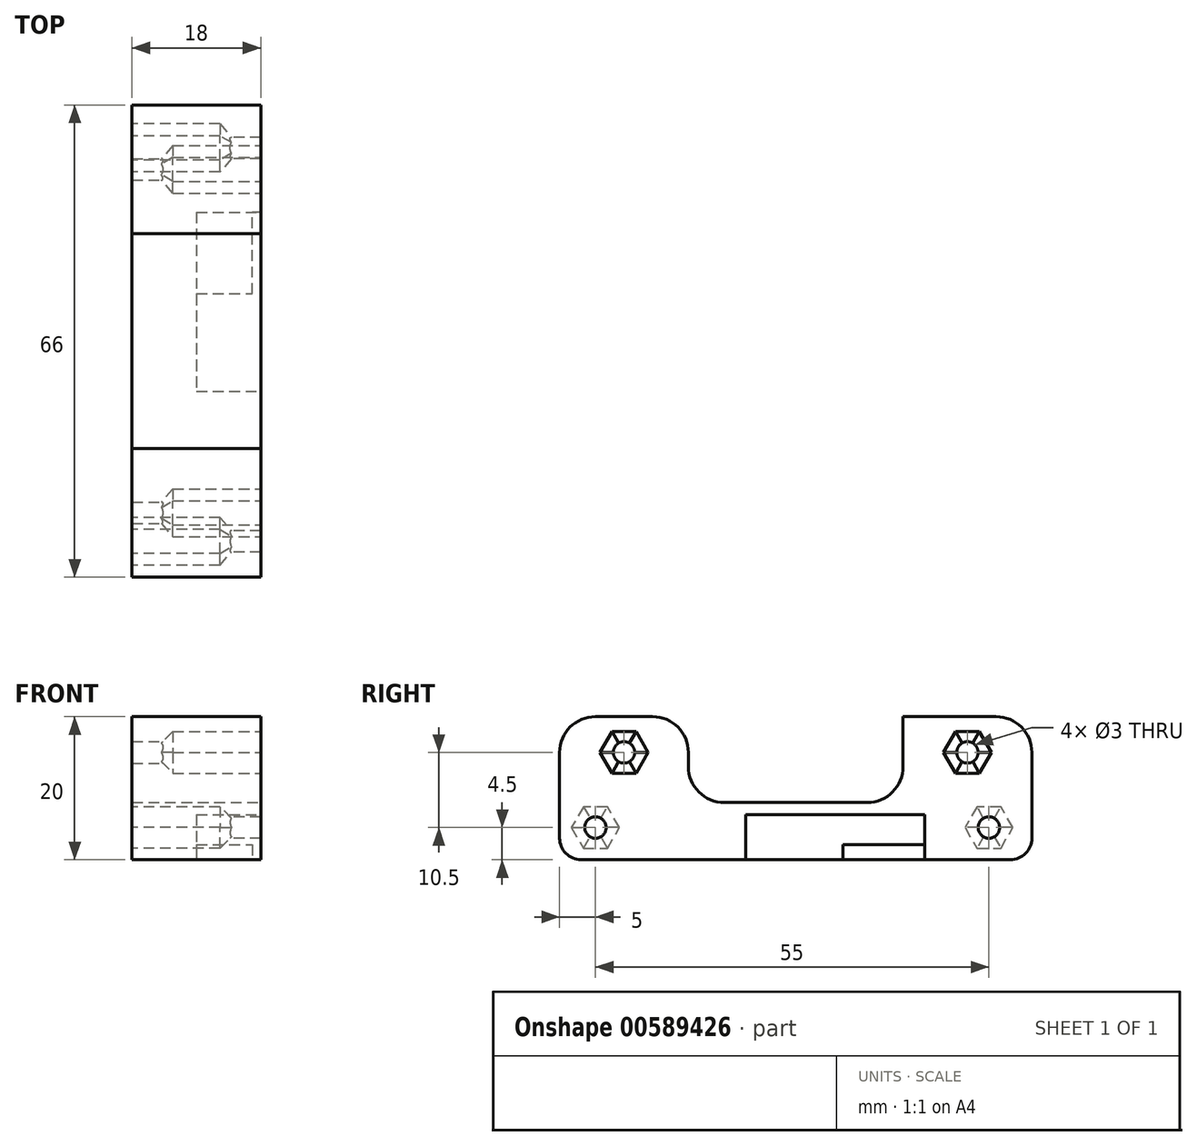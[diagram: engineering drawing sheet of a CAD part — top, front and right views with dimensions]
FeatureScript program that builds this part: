
annotation { "Feature Type Name" : "Feature", "Feature Type Description" : "" }
export const myFeature = defineFeature(function(context is Context, id is Id, definition is map)
    precondition{}
    {
        {
            var Q0;
            Q0=qCreatedBy(makeId("Right.planeOp"),FACE);
            var sketch = newSketch(context, id + "F0", { "sketchPlane" : qUnion([Q0])});
            skLineSegment(sketch, "E0", {"start": v(0, 0) * mm, "end": v(0, 20) * mm});
            skLineSegment(sketch, "E1", {"start": v(0, 20) * mm, "end": v(10, 20) * mm});
            skLineSegment(sketch, "E2", {"start": v(10, 20) * mm, "end": v(10, 18) * mm});
            skLineSegment(sketch, "E3", {"start": v(10, 18) * mm, "end": v(5, 18) * mm});
            skLineSegment(sketch, "E4", {"start": v(5, 18) * mm, "end": v(5, 9) * mm});
            skLineSegment(sketch, "E5", {"start": v(5, 9) * mm, "end": v(66, 9) * mm});
            skLineSegment(sketch, "E6", {"start": v(66, 9) * mm, "end": v(66, 0) * mm});
            skLineSegment(sketch, "E7", {"start": v(66, 0) * mm, "end": v(0, 0) * mm});
            skLineSegment(sketch, "E8", {"start": v(66, 9) * mm, "end": v(66, 20) * mm});
            skLineSegment(sketch, "E9", {"start": v(66, 20) * mm, "end": v(10, 20) * mm});
            skSolve(sketch);
        }
        {
            var Q0;
            Q0=makeQuery(id+"F0.imprint","IMPRINT",FACE,{"disambiguationData":[TD([[makeQuery(id+"F0.imprint","IMPRINT",EDGE,{"derivedFrom":sQuery(id+"F0.wireOp",EDGE,"E0")}),-1.0]])]});
            var Q1;
            Q1=makeQuery(id+"F0.imprint","IMPRINT",FACE,{"disambiguationData":[TD([[makeQuery(id+"F0.imprint","IMPRINT",EDGE,{"derivedFrom":sQuery(id+"F0.wireOp",EDGE,"E2")}),1.0]])]});
            extrude(context, id + "F1", {"entities" : qUnion([Q0, Q1]), "oppositeDirection" : true, "depth" : 16 * mm, "offsetDistance" : 25 * mm});
        }
        {
            var Q0;
            Q0=makeQuery(id+"F1.opExtrude","CAP_FACE",FACE,{"disambiguationData":[OSD([sQuery(id+"F0.wireOp",EDGE,"E0"),sQuery(id+"F0.wireOp",EDGE,"E1"),sQuery(id+"F0.wireOp",EDGE,"E6"),sQuery(id+"F0.wireOp",EDGE,"E7"),sQuery(id+"F0.wireOp",EDGE,"E8"),sQuery(id+"F0.wireOp",EDGE,"E9")])],"isStart":true});
            var sketch = newSketch(context, id + "F2", { "sketchPlane" : qUnion([Q0])});
            skLineSegment(sketch, "E10", {"start": v(51, 6.3) * mm, "end": v(51, 2.1) * mm});
            skLineSegment(sketch, "E11", {"start": v(51, 2.1) * mm, "end": v(39.6, 2.1) * mm});
            skLineSegment(sketch, "E12", {"start": v(39.6, 2.1) * mm, "end": v(39.6, 0) * mm});
            skLineSegment(sketch, "E13", {"start": v(51, 6.3) * mm, "end": v(26, 6.3) * mm});
            skLineSegment(sketch, "E14", {"start": v(26, 6.3) * mm, "end": v(26, 0) * mm});
            skLineSegment(sketch, "E15.0", {"start": v(66, 0) * mm, "end": v(0, 0) * mm});
            skSolve(sketch);
        }
        {
            var Q0;
            Q0=makeQuery(id+"F2.imprint","IMPRINT",FACE,{"disambiguationData":[TD([[makeQuery(id+"F2.imprint","IMPRINT",EDGE,{"derivedFrom":sQuery(id+"F2.wireOp",EDGE,"E10")}),-1.0]])]});
            extrude(context, id + "F3", {"entities" : qUnion([Q0]), "operationType" : NewBodyOperationType.REMOVE, "oppositeDirection" : true, "depth" : 9 * mm, "offsetDistance" : 25 * mm});
        }
        {
            var Q0;
            Q0=makeQuery(id+"F1.opExtrude","SWEPT_FACE",FACE,{"disambiguationData":[OSD([sQuery(id+"F0.wireOp",EDGE,"E7")])]});
            var sketch = newSketch(context, id + "F4", { "sketchPlane" : qUnion([Q0])});
            skLineSegment(sketch, "E16.0", {"start": v(0, -66) * mm, "end": v(0, -39.6) * mm});
            skLineSegment(sketch, "E17.bottom", {"start": v(0, -39.6) * mm, "end": v(-1.2, -39.6) * mm});
            skLineSegment(sketch, "E17.top", {"start": v(0, -51) * mm, "end": v(-1.2, -51) * mm});
            skLineSegment(sketch, "E17.left", {"start": v(0, -39.6) * mm, "end": v(0, -51) * mm});
            skLineSegment(sketch, "E17.right", {"start": v(-1.2, -39.6) * mm, "end": v(-1.2, -51) * mm});
            skPoint(sketch, "E18.0", {"position": v(0, -51) * mm});
            skSolve(sketch);
        }
        {
            var Q0;
            Q0=makeQuery(id+"F4.imprint","IMPRINT",FACE,{"disambiguationData":[TD([[makeQuery(id+"F4.imprint","IMPRINT",EDGE,{"derivedFrom":sQuery(id+"F4.wireOp",EDGE,"E17.bottom")}),-1.0]])]});
            extrude(context, id + "F5", {"entities" : qUnion([Q0]), "operationType" : NewBodyOperationType.REMOVE, "endBound" : BoundingType.UP_TO_NEXT, "oppositeDirection" : true, "depth" : 25 * mm, "offsetDistance" : 25 * mm});
        }
        {
            var Q0;
            Q0=makeQuery(id+"F1.opExtrude","CAP_FACE",FACE,{"disambiguationData":[OSD([sQuery(id+"F0.wireOp",EDGE,"E0"),sQuery(id+"F0.wireOp",EDGE,"E1"),sQuery(id+"F0.wireOp",EDGE,"E2"),sQuery(id+"F0.wireOp",EDGE,"E3"),sQuery(id+"F0.wireOp",EDGE,"E4"),sQuery(id+"F0.wireOp",EDGE,"E5"),sQuery(id+"F0.wireOp",EDGE,"E6"),sQuery(id+"F0.wireOp",EDGE,"E7")])],"isStart":false});
            var sketch = newSketch(context, id + "F6", { "sketchPlane" : qUnion([Q0])});
            skLineSegment(sketch, "E19.0", {"start": v(-66, 0) * mm, "end": v(0, 0) * mm});
            skLineSegment(sketch, "E20.0", {"start": v(0, 0) * mm, "end": v(0, 20) * mm});
            skLineSegment(sketch, "E21", {"start": v(-66, 0) * mm, "end": v(-66, 20) * mm});
            skLineSegment(sketch, "E22", {"start": v(-66, 20) * mm, "end": v(0, 20) * mm});
            skSolve(sketch);
        }
        {
            var Q0;
            {var subQ2=sQuery(id+"F6.wireOp",EDGE,"E19.0");Q0=makeQuery(id+"F6.imprint","IMPRINT",FACE,{"disambiguationData":[TD([[makeQuery(id+"F6.imprint","IMPRINT",EDGE,{"derivedFrom":subQ2}),1.0]])]});}
            var Q1;
            {var subQ0=makeQuery(id+"F1.opExtrude","CAP_EDGE",EDGE,{"disambiguationData":[OSD([sQuery(id+"F0.wireOp",EDGE,"E2")])],"isStart":false});Q1=makeQuery(id+"F6.imprint","IMPRINT",FACE,{"disambiguationData":[TD([[makeQuery(id+"F6.imprint","IMPRINT",EDGE,{"derivedFrom":subQ0}),-1.0]])]});}
            extrude(context, id + "F7", {"entities" : qUnion([Q0, Q1]), "operationType" : NewBodyOperationType.ADD, "depth" : 2 * mm, "offsetDistance" : 25 * mm});
        }
        {
            var Q0;
            Q0=makeQuery(id+"F7.boolean.opBoolean","MERGE",EDGE,{"derivedFrom":[makeQuery(id+"F1.opExtrude","SWEPT_EDGE",EDGE,{"disambiguationData":[OSD([sQuery(id+"F0.wireOp",EDGE,"E6"),sQuery(id+"F0.wireOp",EDGE,"E7")])]}),makeQuery(id+"F7.opExtrude","SWEPT_EDGE",EDGE,{"disambiguationData":[OSD([sQuery(id+"F6.wireOp",EDGE,"E19.0"),sQuery(id+"F6.wireOp",EDGE,"E21")])]})]});
            var Q1;
            Q1=makeQuery(id+"Faa1i12ZNwMVlYs_1.boolean.opBoolean","COPY",EDGE,{"derivedFrom":makeQuery(id+"Faa1i12ZNwMVlYs_1.opExtrude","SWEPT_EDGE",EDGE,{"disambiguationData":[OSD([sQuery(id+"FbflpkZ62X0eoyx_1.wireOp",EDGE,"95200aa5-3b6f-4f71-a4fa-d7a12fe171fd.0"),sQuery(id+"FbflpkZ62X0eoyx_1.wireOp",EDGE,"u4Z3bOsj-DbHr-OVNa-PfcN-1bMwixkQpOJ3")])]})});
            var Q2;
            Q2=makeQuery(id+"F7.boolean.opBoolean","MERGE",EDGE,{"derivedFrom":[makeQuery(id+"F1.opExtrude","SWEPT_EDGE",EDGE,{"disambiguationData":[OSD([sQuery(id+"F0.wireOp",EDGE,"E0"),sQuery(id+"F0.wireOp",EDGE,"E7")])]}),makeQuery(id+"F7.opExtrude","SWEPT_EDGE",EDGE,{"disambiguationData":[OSD([sQuery(id+"F6.wireOp",EDGE,"E19.0"),sQuery(id+"F6.wireOp",EDGE,"E20.0")])]})]});
            fillet(context, id + "F8", {"entities" : qUnion([Q0, Q1, Q2]), "radius" : 3 * mm, "tangentPropagation" : true, "allowEdgeOverflow" : false});
        }
        {
            var Q0;
            Q0=makeQuery(id+"F7.opExtrude","CAP_FACE",FACE,{"disambiguationData":[OSD([sQuery(id+"F6.wireOp",EDGE,"E19.0"),sQuery(id+"F6.wireOp",EDGE,"E20.0"),sQuery(id+"F6.wireOp",EDGE,"E21"),sQuery(id+"F6.wireOp",EDGE,"E22")])],"isStart":false});
            var sketch = newSketch(context, id + "F9", { "sketchPlane" : qUnion([Q0])});
            skCircle(sketch, "E23.cCircle", {"center": v(-60, 4.5) * mm, "radius": 2.9 * mm, "construction": true});
            skLineSegment(sketch, "E23.0", {"start": v(-63.35, 4.5) * mm, "end": v(-61.67, 7.4) * mm});
            skLineSegment(sketch, "E23.1", {"start": v(-61.67, 7.4) * mm, "end": v(-58.33, 7.4) * mm});
            skLineSegment(sketch, "E23.2", {"start": v(-58.33, 7.4) * mm, "end": v(-56.65, 4.5) * mm});
            skLineSegment(sketch, "E23.3", {"start": v(-56.65, 4.5) * mm, "end": v(-58.33, 1.6) * mm});
            skLineSegment(sketch, "E23.4", {"start": v(-58.33, 1.6) * mm, "end": v(-61.67, 1.6) * mm});
            skLineSegment(sketch, "E23.5", {"start": v(-61.67, 1.6) * mm, "end": v(-63.35, 4.5) * mm});
            skPoint(sketch, "E23.0.midPoint", {"position": v(-62.51, 5.95) * mm});
            skLineSegment(sketch, "E24.1.0.0", {"start": v(-6.67, 1.6) * mm, "end": v(-8.35, 4.5) * mm});
            skPoint(sketch, "E24.1.0.1", {"position": v(-7.51, 5.95) * mm});
            skCircle(sketch, "E24.1.0.2", {"center": v(-5, 4.5) * mm, "radius": 2.9 * mm, "construction": true});
            skLineSegment(sketch, "E24.1.0.3", {"start": v(-8.35, 4.5) * mm, "end": v(-6.67, 7.4) * mm});
            skLineSegment(sketch, "E24.1.0.4", {"start": v(-6.67, 7.4) * mm, "end": v(-3.33, 7.4) * mm});
            skLineSegment(sketch, "E24.1.0.5", {"start": v(-3.33, 7.4) * mm, "end": v(-1.65, 4.5) * mm});
            skLineSegment(sketch, "E24.1.0.6", {"start": v(-1.65, 4.5) * mm, "end": v(-3.33, 1.6) * mm});
            skLineSegment(sketch, "E24.1.0.7", {"start": v(-3.33, 1.6) * mm, "end": v(-6.67, 1.6) * mm});
            skLineSegment(sketch, "E24.2.0.0", {"start": v(48.33, 1.6) * mm, "end": v(46.65, 4.5) * mm});
            skPoint(sketch, "E24.2.0.1", {"position": v(47.49, 5.95) * mm});
            skCircle(sketch, "E24.2.0.2", {"center": v(50, 4.5) * mm, "radius": 2.9 * mm, "construction": true});
            skLineSegment(sketch, "E24.2.0.3", {"start": v(46.65, 4.5) * mm, "end": v(48.33, 7.4) * mm});
            skLineSegment(sketch, "E24.2.0.4", {"start": v(48.33, 7.4) * mm, "end": v(51.67, 7.4) * mm});
            skLineSegment(sketch, "E24.2.0.5", {"start": v(51.67, 7.4) * mm, "end": v(53.35, 4.5) * mm});
            skLineSegment(sketch, "E24.2.0.6", {"start": v(53.35, 4.5) * mm, "end": v(51.67, 1.6) * mm});
            skLineSegment(sketch, "E24.2.0.7", {"start": v(51.67, 1.6) * mm, "end": v(48.33, 1.6) * mm});
            skLineSegment(sketch, "E24.direction1", {"start": v(-61.67, 1.6) * mm, "end": v(-6.67, 1.6) * mm, "construction": true});
            skSolve(sketch);
        }
        {
            var Q0;
            Q0=makeQuery(id+"F9.imprint","IMPRINT",FACE,{"disambiguationData":[TD([[makeQuery(id+"F9.imprint","IMPRINT",EDGE,{"derivedFrom":sQuery(id+"F9.wireOp",EDGE,"E23.0")}),-1.0]])]});
            var Q1;
            Q1=makeQuery(id+"F9.imprint","IMPRINT",FACE,{"disambiguationData":[TD([[makeQuery(id+"F9.imprint","IMPRINT",EDGE,{"derivedFrom":sQuery(id+"F9.wireOp",EDGE,"E24.1.0.0")}),-1.0]])]});
            extrude(context, id + "F10", {"entities" : qUnion([Q0, Q1]), "operationType" : NewBodyOperationType.REMOVE, "oppositeDirection" : true, "depth" : 14 * mm, "offsetDistance" : 25 * mm});
        }
        {
            var Q0;
            Q0=makeQuery(id+"F10.boolean.opBoolean","COPY",EDGE,{"derivedFrom":makeQuery(id+"F10.opExtrude","CAP_EDGE",EDGE,{"disambiguationData":[OSD([sQuery(id+"F9.wireOp",EDGE,"E23.0")])],"isStart":false})});
            var Q1;
            Q1=makeQuery(id+"F10.boolean.opBoolean","COPY",EDGE,{"derivedFrom":makeQuery(id+"F10.opExtrude","CAP_EDGE",EDGE,{"disambiguationData":[OSD([sQuery(id+"F9.wireOp",EDGE,"E23.1")])],"isStart":false})});
            var Q2;
            Q2=makeQuery(id+"F10.boolean.opBoolean","COPY",EDGE,{"derivedFrom":makeQuery(id+"F10.opExtrude","CAP_EDGE",EDGE,{"disambiguationData":[OSD([sQuery(id+"F9.wireOp",EDGE,"E23.5")])],"isStart":false})});
            var Q3;
            Q3=makeQuery(id+"F10.boolean.opBoolean","COPY",FACE,{"derivedFrom":makeQuery(id+"F10.opExtrude","CAP_FACE",FACE,{"disambiguationData":[OSD([sQuery(id+"F9.wireOp",EDGE,"E23.0"),sQuery(id+"F9.wireOp",EDGE,"E23.1"),sQuery(id+"F9.wireOp",EDGE,"E23.2"),sQuery(id+"F9.wireOp",EDGE,"E23.3"),sQuery(id+"F9.wireOp",EDGE,"E23.4"),sQuery(id+"F9.wireOp",EDGE,"E23.5")])],"isStart":false})});
            var Q4;
            Q4=makeQuery(id+"F10.boolean.opBoolean","COPY",FACE,{"derivedFrom":makeQuery(id+"F10.opExtrude","CAP_FACE",FACE,{"disambiguationData":[OSD([sQuery(id+"F9.wireOp",EDGE,"E24.1.0.0"),sQuery(id+"F9.wireOp",EDGE,"E24.1.0.3"),sQuery(id+"F9.wireOp",EDGE,"E24.1.0.4"),sQuery(id+"F9.wireOp",EDGE,"E24.1.0.5"),sQuery(id+"F9.wireOp",EDGE,"E24.1.0.6"),sQuery(id+"F9.wireOp",EDGE,"E24.1.0.7")])],"isStart":false})});
            chamfer(context, id + "F11", {"entities" : qUnion([Q0, Q1, Q2, Q3, Q4]), "width" : 1.7 * mm, "tangentPropagation" : true});
        }
        {
            var Q0;
            Q0=makeQuery(id+"F7.opExtrude","CAP_FACE",FACE,{"disambiguationData":[OSD([sQuery(id+"F6.wireOp",EDGE,"E19.0"),sQuery(id+"F6.wireOp",EDGE,"E20.0"),sQuery(id+"F6.wireOp",EDGE,"E21"),sQuery(id+"F6.wireOp",EDGE,"E22")])],"isStart":false});
            var sketch = newSketch(context, id + "F12", { "sketchPlane" : qUnion([Q0])});
            skPoint(sketch, "E25.0", {"position": v(-60, 1.6) * mm});
            skPoint(sketch, "E26.0", {"position": v(-60, 7.4) * mm});
            skLineSegment(sketch, "E27", {"start": v(-60, 7.4) * mm, "end": v(-60, 1.6) * mm, "construction": true});
            skPoint(sketch, "E28", {"position": v(-60, 4.5) * mm});
            skPoint(sketch, "E29.0", {"position": v(-5, 7.4) * mm});
            skPoint(sketch, "E30.0", {"position": v(-5, 1.6) * mm});
            skLineSegment(sketch, "E31", {"start": v(-5, 7.4) * mm, "end": v(-5, 1.6) * mm, "construction": true});
            skPoint(sketch, "E32", {"position": v(-5, 4.5) * mm});
            skSolve(sketch);
        }
        {
            var Q0;
            Q0=sQuery(id+"F12.wireOp",VERTEX,"E28");
            var Q1;
            Q1=sQuery(id+"F12.wireOp",VERTEX,"E32");
            var Q2;
            Q2=makeQuery(id+"F1.opExtrude","SWEPT_BODY",BODY,{"disambiguationData":[OSD([sQuery(id+"F0.wireOp",EDGE,"E0"),sQuery(id+"F0.wireOp",EDGE,"E1"),sQuery(id+"F0.wireOp",EDGE,"E2"),sQuery(id+"F0.wireOp",EDGE,"E3"),sQuery(id+"F0.wireOp",EDGE,"E4"),sQuery(id+"F0.wireOp",EDGE,"E5"),sQuery(id+"F0.wireOp",EDGE,"E6"),sQuery(id+"F0.wireOp",EDGE,"E7")])]});
            hole(context, id + "F13", {"style" : HoleStyle.SIMPLE, "endStyle" : HoleEndStyle.THROUGH, "holeDiameter" : 3 * mm, "isTappedThrough" : true, "tappedDepth" : 12 * mm, "tapClearance" : 3, "locations" : qUnion([Q0, Q1]), "scope" : qUnion([Q2])});
        }
        {
            var Q0;
            Q0=makeQuery(id+"F7.boolean.opBoolean","MERGE",EDGE,{"derivedFrom":[makeQuery(id+"F1.opExtrude","SWEPT_EDGE",EDGE,{"disambiguationData":[OSD([sQuery(id+"F0.wireOp",EDGE,"E8"),sQuery(id+"F0.wireOp",EDGE,"E9")])]}),makeQuery(id+"F7.opExtrude","SWEPT_EDGE",EDGE,{"disambiguationData":[OSD([sQuery(id+"F6.wireOp",EDGE,"E21"),sQuery(id+"F6.wireOp",EDGE,"E22")])]})]});
            var Q1;
            Q1=makeQuery(id+"F7.boolean.opBoolean","MERGE",EDGE,{"derivedFrom":[makeQuery(id+"F1.opExtrude","SWEPT_EDGE",EDGE,{"disambiguationData":[OSD([sQuery(id+"F0.wireOp",EDGE,"E0"),sQuery(id+"F0.wireOp",EDGE,"E1")])]}),makeQuery(id+"F7.opExtrude","SWEPT_EDGE",EDGE,{"disambiguationData":[OSD([sQuery(id+"F6.wireOp",EDGE,"E20.0"),sQuery(id+"F6.wireOp",EDGE,"E22")])]})]});
            fillet(context, id + "F14", {"entities" : qUnion([Q0, Q1]), "radius" : 5 * mm, "tangentPropagation" : true, "allowEdgeOverflow" : false});
        }
        {
            var Q0;
            Q0=makeQuery(id+"F1.opExtrude","CAP_FACE",FACE,{"disambiguationData":[OSD([sQuery(id+"F0.wireOp",EDGE,"E0"),sQuery(id+"F0.wireOp",EDGE,"E1"),sQuery(id+"F0.wireOp",EDGE,"E6"),sQuery(id+"F0.wireOp",EDGE,"E7"),sQuery(id+"F0.wireOp",EDGE,"E8"),sQuery(id+"F0.wireOp",EDGE,"E9")])],"isStart":true});
            var sketch = newSketch(context, id + "F15", { "sketchPlane" : qUnion([Q0])});
            skLineSegment(sketch, "E33", {"start": v(57, 15) * mm, "end": v(9, 15) * mm});
            skPoint(sketch, "E34.0", {"position": v(33, 20) * mm});
            skLineSegment(sketch, "E35", {"start": v(33, 20) * mm, "end": v(33, 15) * mm, "construction": true});
            skSolve(sketch);
        }
        {
            var Q0;
            Q0=sQuery(id+"F15.wireOp",VERTEX,"E33.start");
            var Q1;
            Q1=sQuery(id+"F15.wireOp",VERTEX,"E33.end");
            var Q2;
            Q2=makeQuery(id+"F1.opExtrude","SWEPT_BODY",BODY,{"disambiguationData":[OSD([sQuery(id+"F0.wireOp",EDGE,"E0"),sQuery(id+"F0.wireOp",EDGE,"E1"),sQuery(id+"F0.wireOp",EDGE,"E6"),sQuery(id+"F0.wireOp",EDGE,"E7"),sQuery(id+"F0.wireOp",EDGE,"E8"),sQuery(id+"F0.wireOp",EDGE,"E9")])]});
            hole(context, id + "F16", {"style" : HoleStyle.SIMPLE, "endStyle" : HoleEndStyle.THROUGH, "holeDiameter" : 3 * mm, "isTappedThrough" : true, "tappedDepth" : 12 * mm, "tapClearance" : 3, "locations" : qUnion([Q0, Q1]), "scope" : qUnion([Q2])});
        }
        {
            var Q0;
            Q0=makeQuery(id+"F1.opExtrude","CAP_FACE",FACE,{"disambiguationData":[OSD([sQuery(id+"F0.wireOp",EDGE,"E0"),sQuery(id+"F0.wireOp",EDGE,"E1"),sQuery(id+"F0.wireOp",EDGE,"E6"),sQuery(id+"F0.wireOp",EDGE,"E7"),sQuery(id+"F0.wireOp",EDGE,"E8"),sQuery(id+"F0.wireOp",EDGE,"E9")])],"isStart":true});
            var sketch = newSketch(context, id + "F17", { "sketchPlane" : qUnion([Q0])});
            skCircle(sketch, "E36.0", {"center": v(57, 15) * mm, "radius": 1.5 * mm});
            skCircle(sketch, "E37.0", {"center": v(9, 15) * mm, "radius": 1.5 * mm});
            skCircle(sketch, "E38.cCircle", {"center": v(57, 15) * mm, "radius": 2.9 * mm, "construction": true});
            skLineSegment(sketch, "E38.0", {"start": v(60.35, 15) * mm, "end": v(58.67, 12.1) * mm});
            skLineSegment(sketch, "E38.1", {"start": v(58.67, 12.1) * mm, "end": v(55.33, 12.1) * mm});
            skLineSegment(sketch, "E38.2", {"start": v(55.33, 12.1) * mm, "end": v(53.65, 15) * mm});
            skLineSegment(sketch, "E38.3", {"start": v(53.65, 15) * mm, "end": v(55.33, 17.9) * mm});
            skLineSegment(sketch, "E38.4", {"start": v(55.33, 17.9) * mm, "end": v(58.67, 17.9) * mm});
            skLineSegment(sketch, "E38.5", {"start": v(58.67, 17.9) * mm, "end": v(60.35, 15) * mm});
            skPoint(sketch, "E38.0.midPoint", {"position": v(59.51, 13.55) * mm});
            skCircle(sketch, "E39.cCircle", {"center": v(9, 15) * mm, "radius": 2.9 * mm, "construction": true});
            skLineSegment(sketch, "E39.0", {"start": v(12.35, 15) * mm, "end": v(10.67, 12.1) * mm});
            skLineSegment(sketch, "E39.1", {"start": v(10.67, 12.1) * mm, "end": v(7.33, 12.1) * mm});
            skLineSegment(sketch, "E39.2", {"start": v(7.33, 12.1) * mm, "end": v(5.65, 15) * mm});
            skLineSegment(sketch, "E39.3", {"start": v(5.65, 15) * mm, "end": v(7.33, 17.9) * mm});
            skLineSegment(sketch, "E39.4", {"start": v(7.33, 17.9) * mm, "end": v(10.67, 17.9) * mm});
            skLineSegment(sketch, "E39.5", {"start": v(10.67, 17.9) * mm, "end": v(12.35, 15) * mm});
            skPoint(sketch, "E39.0.midPoint", {"position": v(11.51, 13.55) * mm});
            skSolve(sketch);
        }
        {
            var Q0;
            Q0=makeQuery(id+"F17.imprint","IMPRINT",FACE,{"disambiguationData":[TD([[makeQuery(id+"F17.imprint","IMPRINT",EDGE,{"derivedFrom":sQuery(id+"F17.wireOp",EDGE,"E37.0")}),-1.0]])]});
            var Q1;
            Q1=makeQuery(id+"F17.imprint","IMPRINT",FACE,{"disambiguationData":[TD([[makeQuery(id+"F17.imprint","IMPRINT",EDGE,{"derivedFrom":sQuery(id+"F17.wireOp",EDGE,"E36.0")}),-1.0]])]});
            extrude(context, id + "F18", {"entities" : qUnion([Q0, Q1]), "operationType" : NewBodyOperationType.REMOVE, "oppositeDirection" : true, "depth" : 14 * mm, "offsetDistance" : 25 * mm});
        }
        {
            var Q0;
            Q0=makeQuery(id+"F18.boolean.opBoolean","COPY",EDGE,{"derivedFrom":makeQuery(id+"F18.opExtrude","CAP_EDGE",EDGE,{"disambiguationData":[OSD([sQuery(id+"F17.wireOp",EDGE,"E38.0")])],"isStart":false})});
            var Q1;
            Q1=makeQuery(id+"F18.boolean.opBoolean","COPY",EDGE,{"derivedFrom":makeQuery(id+"F18.opExtrude","CAP_EDGE",EDGE,{"disambiguationData":[OSD([sQuery(id+"F17.wireOp",EDGE,"E38.5")])],"isStart":false})});
            var Q2;
            Q2=makeQuery(id+"F18.boolean.opBoolean","COPY",EDGE,{"derivedFrom":makeQuery(id+"F18.opExtrude","CAP_EDGE",EDGE,{"disambiguationData":[OSD([sQuery(id+"F17.wireOp",EDGE,"E38.4")])],"isStart":false})});
            var Q3;
            Q3=makeQuery(id+"F18.boolean.opBoolean","COPY",EDGE,{"derivedFrom":makeQuery(id+"F18.opExtrude","CAP_EDGE",EDGE,{"disambiguationData":[OSD([sQuery(id+"F17.wireOp",EDGE,"E38.3")])],"isStart":false})});
            var Q4;
            Q4=makeQuery(id+"F18.boolean.opBoolean","COPY",EDGE,{"derivedFrom":makeQuery(id+"F18.opExtrude","CAP_EDGE",EDGE,{"disambiguationData":[OSD([sQuery(id+"F17.wireOp",EDGE,"E38.2")])],"isStart":false})});
            var Q5;
            Q5=makeQuery(id+"F18.boolean.opBoolean","COPY",EDGE,{"derivedFrom":makeQuery(id+"F18.opExtrude","CAP_EDGE",EDGE,{"disambiguationData":[OSD([sQuery(id+"F17.wireOp",EDGE,"E38.1")])],"isStart":false})});
            var Q6;
            Q6=makeQuery(id+"F18.boolean.opBoolean","COPY",EDGE,{"derivedFrom":makeQuery(id+"F18.opExtrude","CAP_EDGE",EDGE,{"disambiguationData":[OSD([sQuery(id+"F17.wireOp",EDGE,"E39.1")])],"isStart":false})});
            var Q7;
            Q7=makeQuery(id+"F18.boolean.opBoolean","COPY",EDGE,{"derivedFrom":makeQuery(id+"F18.opExtrude","CAP_EDGE",EDGE,{"disambiguationData":[OSD([sQuery(id+"F17.wireOp",EDGE,"E39.0")])],"isStart":false})});
            var Q8;
            Q8=makeQuery(id+"F18.boolean.opBoolean","COPY",EDGE,{"derivedFrom":makeQuery(id+"F18.opExtrude","CAP_EDGE",EDGE,{"disambiguationData":[OSD([sQuery(id+"F17.wireOp",EDGE,"E39.5")])],"isStart":false})});
            var Q9;
            Q9=makeQuery(id+"F18.boolean.opBoolean","COPY",EDGE,{"derivedFrom":makeQuery(id+"F18.opExtrude","CAP_EDGE",EDGE,{"disambiguationData":[OSD([sQuery(id+"F17.wireOp",EDGE,"E39.4")])],"isStart":false})});
            var Q10;
            Q10=makeQuery(id+"F18.boolean.opBoolean","COPY",EDGE,{"derivedFrom":makeQuery(id+"F18.opExtrude","CAP_EDGE",EDGE,{"disambiguationData":[OSD([sQuery(id+"F17.wireOp",EDGE,"E39.3")])],"isStart":false})});
            var Q11;
            Q11=makeQuery(id+"F18.boolean.opBoolean","COPY",EDGE,{"derivedFrom":makeQuery(id+"F18.opExtrude","CAP_EDGE",EDGE,{"disambiguationData":[OSD([sQuery(id+"F17.wireOp",EDGE,"E39.2")])],"isStart":false})});
            chamfer(context, id + "F19", {"entities" : qUnion([Q0, Q1, Q2, Q3, Q4, Q5, Q6, Q7, Q8, Q9, Q10, Q11]), "width" : 1.7 * mm, "tangentPropagation" : true});
        }
        {
            var Q0;
            Q0=makeQuery(id+"F1.opExtrude","CAP_FACE",FACE,{"disambiguationData":[OSD([sQuery(id+"F0.wireOp",EDGE,"E0"),sQuery(id+"F0.wireOp",EDGE,"E1"),sQuery(id+"F0.wireOp",EDGE,"E6"),sQuery(id+"F0.wireOp",EDGE,"E7"),sQuery(id+"F0.wireOp",EDGE,"E8"),sQuery(id+"F0.wireOp",EDGE,"E9")])],"isStart":true});
            var sketch = newSketch(context, id + "F20", { "sketchPlane" : qUnion([Q0])});
            skLineSegment(sketch, "E40.bottom", {"start": v(48, 20) * mm, "end": v(18, 20) * mm});
            skLineSegment(sketch, "E40.top", {"start": v(48, 8) * mm, "end": v(18, 8) * mm});
            skLineSegment(sketch, "E40.left", {"start": v(48, 20) * mm, "end": v(48, 8) * mm});
            skLineSegment(sketch, "E40.right", {"start": v(18, 20) * mm, "end": v(18, 8) * mm});
            skPoint(sketch, "E41.0", {"position": v(33, 20) * mm});
            skSolve(sketch);
        }
        {
            var Q0;
            Q0=makeQuery(id+"F20.imprint","IMPRINT",FACE,{"disambiguationData":[TD([[makeQuery(id+"F20.imprint","IMPRINT",EDGE,{"derivedFrom":sQuery(id+"F20.wireOp",EDGE,"E40.bottom")}),-1.0]])]});
            extrude(context, id + "F21", {"entities" : qUnion([Q0]), "operationType" : NewBodyOperationType.REMOVE, "endBound" : BoundingType.THROUGH_ALL, "oppositeDirection" : true, "depth" : 25 * mm, "offsetDistance" : 25 * mm});
        }
        {
            var Q0;
            Q0=makeQuery(id+"F21.boolean.opBoolean","COPY",EDGE,{"derivedFrom":makeQuery(id+"F21.opExtrude","SWEPT_EDGE",EDGE,{"disambiguationData":[OSD([sQuery(id+"F0.wireOp",EDGE,"E1"),sQuery(id+"F0.wireOp",EDGE,"E9"),sQuery(id+"F20.wireOp",EDGE,"E40.bottom"),sQuery(id+"F20.wireOp",EDGE,"E40.left")])]})});
            var Q1;
            Q1=makeQuery(id+"F21.boolean.opBoolean","COPY",EDGE,{"derivedFrom":makeQuery(id+"F21.opExtrude","SWEPT_EDGE",EDGE,{"disambiguationData":[OSD([sQuery(id+"F0.wireOp",EDGE,"E1"),sQuery(id+"F0.wireOp",EDGE,"E9"),sQuery(id+"F20.wireOp",EDGE,"E40.bottom"),sQuery(id+"F20.wireOp",EDGE,"E40.right")])]})});
            fillet(context, id + "F22", {"entities" : qUnion([Q0, Q1]), "radius" : 5 * mm, "tangentPropagation" : true, "allowEdgeOverflow" : false});
        }
        {
            var Q0;
            Q0=makeQuery(id+"F21.boolean.opBoolean","COPY",EDGE,{"derivedFrom":makeQuery(id+"F21.opExtrude","SWEPT_EDGE",EDGE,{"disambiguationData":[OSD([sQuery(id+"F20.wireOp",EDGE,"E40.top"),sQuery(id+"F20.wireOp",EDGE,"E40.left")])]})});
            var Q1;
            Q1=makeQuery(id+"F21.boolean.opBoolean","COPY",EDGE,{"derivedFrom":makeQuery(id+"F21.opExtrude","SWEPT_EDGE",EDGE,{"disambiguationData":[OSD([sQuery(id+"F20.wireOp",EDGE,"E40.top"),sQuery(id+"F20.wireOp",EDGE,"E40.right")])]})});
            fillet(context, id + "F23", {"entities" : qUnion([Q0, Q1]), "radius" : 5 * mm, "tangentPropagation" : true, "allowEdgeOverflow" : false});
        }
    });
